# Revit family: Hydrant_Wall_Narrow-Zurn-Z1350-EZ-with_Mounting_Brackets
name_source: partatom
category: Plumbing Fixtures
units: mm (PartAtom-declared; Revit-internal decimal feet)

## family parameters
Cut with Voids When Loaded = No
Host = Face
Maintain Annotation Orientation = No
OmniClass Number = 23.65.70.00
OmniClass Title = Terminals for Supplied Liquids and Gases
Part Type = Normal
Room Calculation Point = No
Round Connector Dimension = Use Radius
Shared = No

## types (1)
- Z1350-EZ
    Assembly Code = D2020100
    Body = Bronze - Zurn - Polished
    CW Connection = Yes
    CWFU = 1
    Default Elevation = 48 "
    Description = Narrow Wall Hydrant With Mounting Brackets Encased, Moderate Climate
    HW Connection = No
    HWFU = 0
    Installation instructions = https://files.zurn.com
    Manufacturer = Zurn Water, LLC
    Manufacturer Brand = Zurn
    Model = Z1327-EZ
    Modified Date = 10/17/2025
    Nominal Radius = 0.375 "
    Product Documentation Link = http://www.zurn.com
    Product Page URL = http://www.zurn.com
    Product data url = https://bimobject.com
    URL = http://www.zurn.com
    Vent Connection = No
    WFU = 0
    Waste Connection = No

## geometry (parser evidence)
native form markers: Blend x4, Sweep x15
no freeform markers — native parametric forms only
